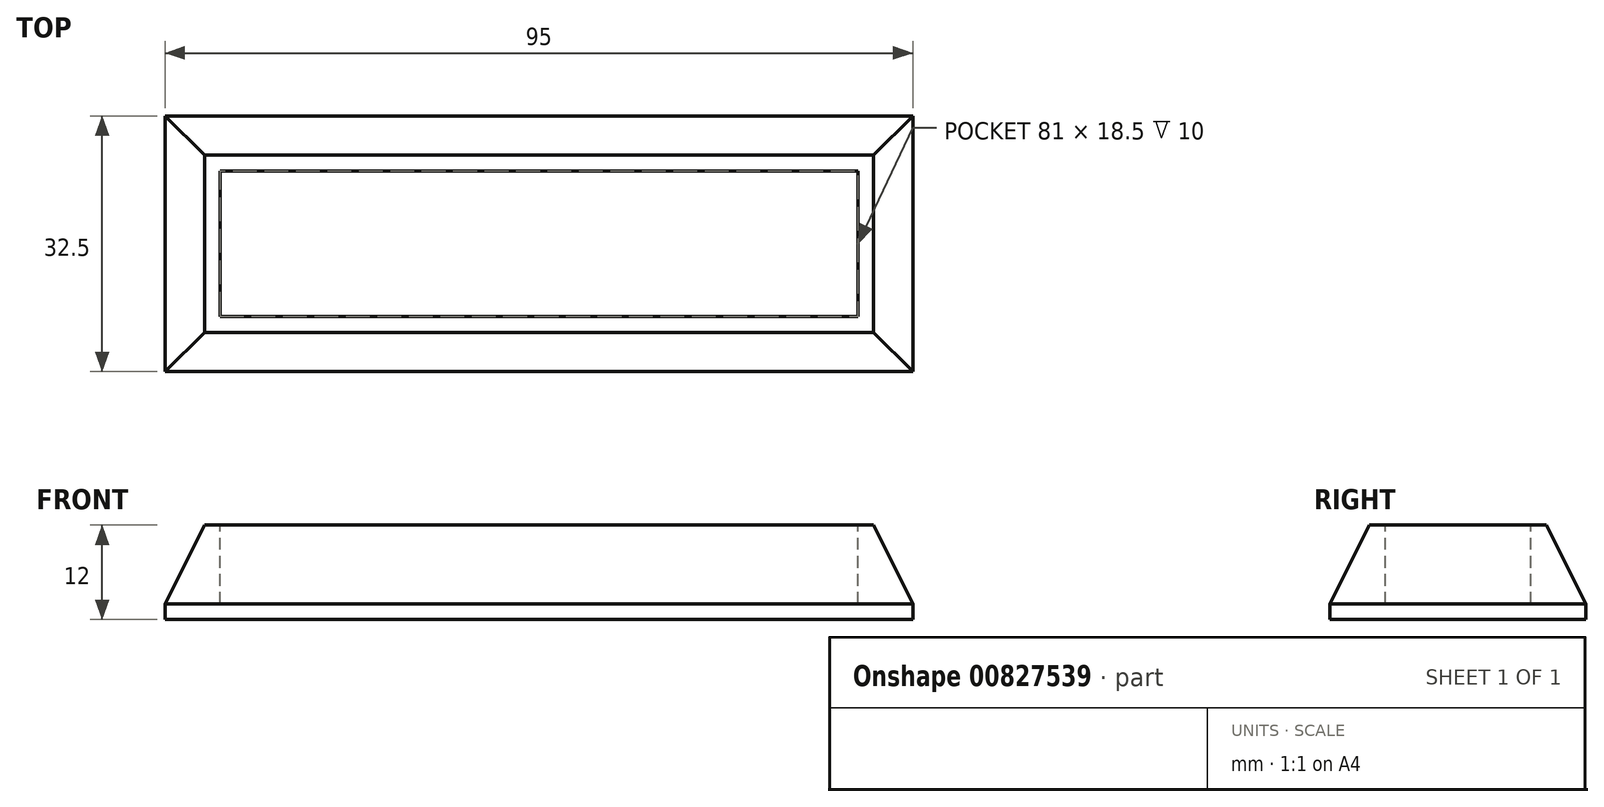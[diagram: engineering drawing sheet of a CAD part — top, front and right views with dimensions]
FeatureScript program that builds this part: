
annotation { "Feature Type Name" : "Feature", "Feature Type Description" : "" }
export const myFeature = defineFeature(function(context is Context, id is Id, definition is map)
    precondition{}
    {
        {
            var Q0;
            Q0=qCreatedBy(makeId("Top.planeOp"),FACE);
            var sketch = newSketch(context, id + "F0", { "sketchPlane" : qUnion([Q0])});
            skLineSegment(sketch, "E0", {"start": v(0, 18.5) * mm, "end": v(0, 25.5) * mm, "construction": true});
            skLineSegment(sketch, "E1", {"start": v(81, 0) * mm, "end": v(88, 0) * mm, "construction": true});
            skLineSegment(sketch, "E2", {"start": v(0, 25.5) * mm, "end": v(-7, 25.5) * mm, "construction": true});
            skLineSegment(sketch, "E3", {"start": v(88, 0) * mm, "end": v(88, -7) * mm, "construction": true});
            skLineSegment(sketch, "E4.bottom", {"start": v(-7, 25.5) * mm, "end": v(88, 25.5) * mm});
            skLineSegment(sketch, "E4.top", {"start": v(-7, -7) * mm, "end": v(88, -7) * mm});
            skLineSegment(sketch, "E4.left", {"start": v(-7, 25.5) * mm, "end": v(-7, -7) * mm});
            skLineSegment(sketch, "E4.right", {"start": v(88, 25.5) * mm, "end": v(88, -7) * mm});
            skLineSegment(sketch, "E5.bottom", {"start": v(0, 18.5) * mm, "end": v(81, 18.5) * mm, "construction": true});
            skLineSegment(sketch, "E5.top", {"start": v(0, 0) * mm, "end": v(81, 0) * mm, "construction": true});
            skLineSegment(sketch, "E5.left", {"start": v(0, 18.5) * mm, "end": v(0, 0) * mm, "construction": true});
            skLineSegment(sketch, "E5.right", {"start": v(81, 18.5) * mm, "end": v(81, 0) * mm, "construction": true});
            skSolve(sketch);
        }
        {
            var Q0;
            Q0 = qSketchRegion(id + "F0", true);
            extrude(context, id + "F1", {"entities" : qUnion([Q0]), "depth" : 12 * mm, "offsetDistance" : 25 * mm});
        }
        {
            var Q0;
            Q0=makeQuery(id+"F1.opExtrude","CAP_FACE",FACE,{"disambiguationData":[OSD([sQuery(id+"F0.wireOp",EDGE,"E4.bottom"),sQuery(id+"F0.wireOp",EDGE,"E4.top"),sQuery(id+"F0.wireOp",EDGE,"E4.left"),sQuery(id+"F0.wireOp",EDGE,"E4.right")])],"isStart":false});
            var sketch = newSketch(context, id + "F2", { "sketchPlane" : qUnion([Q0])});
            skLineSegment(sketch, "E6.bottom", {"start": v(0, 0) * mm, "end": v(4.93, 0) * mm});
            skLineSegment(sketch, "E6.top", {"start": v(0, 0) * mm, "end": v(4.93, 0) * mm});
            skLineSegment(sketch, "E6.left", {"start": v(0, 0) * mm, "end": v(0, 0) * mm});
            skLineSegment(sketch, "E6.right", {"start": v(4.93, 0) * mm, "end": v(4.93, 0) * mm});
            skLineSegment(sketch, "E7.bottom", {"start": v(0, 0) * mm, "end": v(81, 0) * mm});
            skLineSegment(sketch, "E7.top", {"start": v(0, 18.5) * mm, "end": v(81, 18.5) * mm});
            skLineSegment(sketch, "E7.left", {"start": v(0, 0) * mm, "end": v(0, 18.5) * mm});
            skLineSegment(sketch, "E7.right", {"start": v(81, 0) * mm, "end": v(81, 18.5) * mm});
            skSolve(sketch);
        }
        {
            var Q0;
            Q0 = qSketchRegion(id + "F2", true);
            extrude(context, id + "F3", {"entities" : qUnion([Q0]), "operationType" : NewBodyOperationType.REMOVE, "oppositeDirection" : true, "depth" : 10 * mm, "offsetDistance" : 25 * mm});
        }
        {
            var Q0;
            Q0=makeQuery(id+"F1.opExtrude","CAP_EDGE",EDGE,{"disambiguationData":[OSD([sQuery(id+"F0.wireOp",EDGE,"E4.bottom")])],"isStart":false});
            var Q1;
            Q1=makeQuery(id+"F1.opExtrude","CAP_EDGE",EDGE,{"disambiguationData":[OSD([sQuery(id+"F0.wireOp",EDGE,"E4.right")])],"isStart":false});
            var Q2;
            Q2=makeQuery(id+"F1.opExtrude","CAP_EDGE",EDGE,{"disambiguationData":[OSD([sQuery(id+"F0.wireOp",EDGE,"E4.top")])],"isStart":false});
            var Q3;
            Q3=makeQuery(id+"F1.opExtrude","CAP_EDGE",EDGE,{"disambiguationData":[OSD([sQuery(id+"F0.wireOp",EDGE,"E4.left")])],"isStart":false});
            chamfer(context, id + "F4", {"entities" : qUnion([Q0, Q1, Q2, Q3]), "chamferType" : ChamferType.TWO_OFFSETS, "width1" : 10 * mm, "oppositeDirection" : false, "width2" : 5 * mm, "tangentPropagation" : true});
        }
    });
